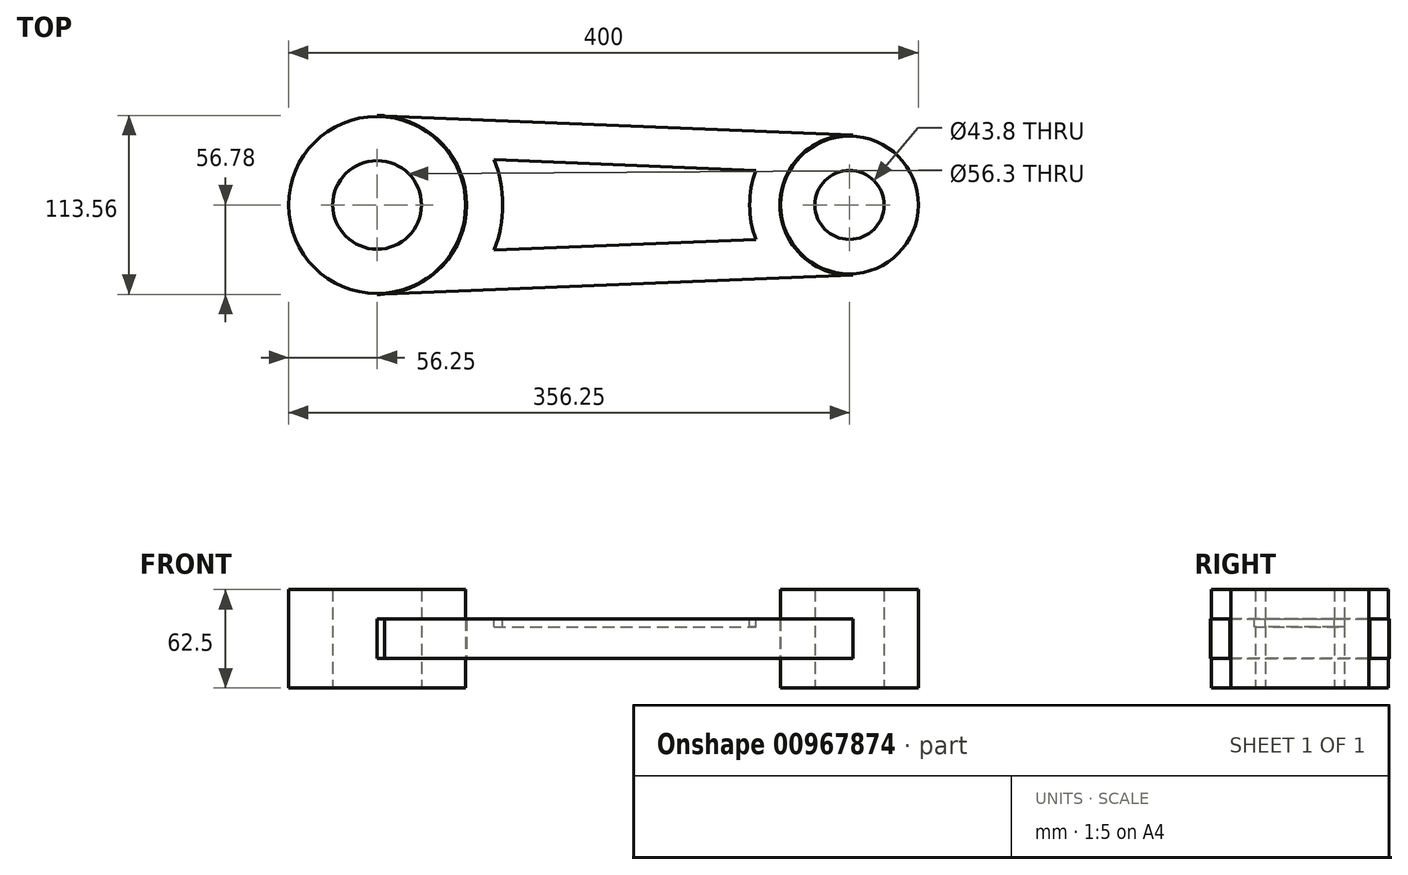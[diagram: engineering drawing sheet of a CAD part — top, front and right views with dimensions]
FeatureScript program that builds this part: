
annotation { "Feature Type Name" : "Feature", "Feature Type Description" : "" }
export const myFeature = defineFeature(function(context is Context, id is Id, definition is map)
    precondition{}
    {
        {
            var Q0;
            Q0=qCreatedBy(makeId("Top.planeOp"),FACE);
            var sketch = newSketch(context, id + "F0", { "sketchPlane" : qUnion([Q0])});
            skCircle(sketch, "E0", {"center": v(0, 0) * mm, "radius": 28.15 * mm});
            skCircle(sketch, "E1", {"center": v(0, 0) * mm, "radius": 56.25 * mm});
            skLineSegment(sketch, "E2", {"start": v(0, 0) * mm, "end": v(300, 0) * mm, "construction": true});
            skCircle(sketch, "E3", {"center": v(300, 0) * mm, "radius": 21.9 * mm});
            skCircle(sketch, "E4", {"center": v(300, 0) * mm, "radius": 43.75 * mm});
            skSolve(sketch);
        }
        {
            var Q0;
            Q0 = qSketchRegion(id + "F0", true);
            extrude(context, id + "F1", {"entities" : qUnion([Q0]), "endBound" : BoundingType.SYMMETRIC, "depth" : 62.5 * mm, "offsetDistance" : 25 * mm});
        }
        {
            var Q0;
            Q0=qCreatedBy(makeId("Top.planeOp"),FACE);
            var sketch = newSketch(context, id + "F2", { "sketchPlane" : qUnion([Q0])});
            skArc(sketch, "E5", {"start": v(0, -56.78) * mm, "mid": v(56.78, 0) * mm, "end": v(0, 56.78) * mm});
            skArc(sketch, "E6", {"start": v(302.19, 44.44) * mm, "mid": v(255.9, 0) * mm, "end": v(302.19, -44.44) * mm});
            skLineSegment(sketch, "E7", {"start": v(0, 56.78) * mm, "end": v(302.19, 44.44) * mm});
            skLineSegment(sketch, "E8", {"start": v(0, -56.78) * mm, "end": v(302.19, -44.44) * mm});
            skSolve(sketch);
        }
        {
            var Q0;
            Q0 = qSketchRegion(id + "F2", true);
            extrude(context, id + "F3", {"entities" : qUnion([Q0]), "endBound" : BoundingType.SYMMETRIC, "depth" : 25 * mm, "offsetDistance" : 25 * mm});
        }
        {
            var Q0;
            Q0=makeQuery(id+"F3.opExtrude","CAP_FACE",FACE,{"disambiguationData":[OSD([sQuery(id+"F2.wireOp",EDGE,"E5"),sQuery(id+"F2.wireOp",EDGE,"E6"),sQuery(id+"F2.wireOp",EDGE,"E7"),sQuery(id+"F2.wireOp",EDGE,"E8")])],"isStart":false});
            var sketch = newSketch(context, id + "F4", { "sketchPlane" : qUnion([Q0])});
            skArc(sketch, "E9", {"start": v(74.19, -28.73) * mm, "mid": v(79.8, 0) * mm, "end": v(74.19, 28.73) * mm});
            skArc(sketch, "E10", {"start": v(240.52, 21.94) * mm, "mid": v(236.63, 0) * mm, "end": v(240.52, -21.94) * mm});
            skLineSegment(sketch, "E11.0", {"start": v(74.19, 28.73) * mm, "end": v(240.52, 21.94) * mm});
            skLineSegment(sketch, "E12.trimOffspring", {"start": v(74.19, -28.73) * mm, "end": v(240.52, -21.94) * mm});
            skPoint(sketch, "E13.MirrorCS.start.orphan", {"position": v(3.6, -31.6) * mm});
            skPoint(sketch, "E14.orphan", {"position": v(3.6, 31.6) * mm});
            skSolve(sketch);
        }
        {
            var Q0;
            Q0=makeQuery(id+"F4.imprint","IMPRINT",FACE,{"disambiguationData":[TD([[makeQuery(id+"F4.imprint","IMPRINT",EDGE,{"derivedFrom":sQuery(id+"F4.wireOp",EDGE,"E9")}),-1.0]])]});
            extrude(context, id + "F5", {"entities" : qUnion([Q0]), "operationType" : NewBodyOperationType.REMOVE, "oppositeDirection" : true, "depth" : 5 * mm, "offsetDistance" : 25 * mm});
        }
    });
